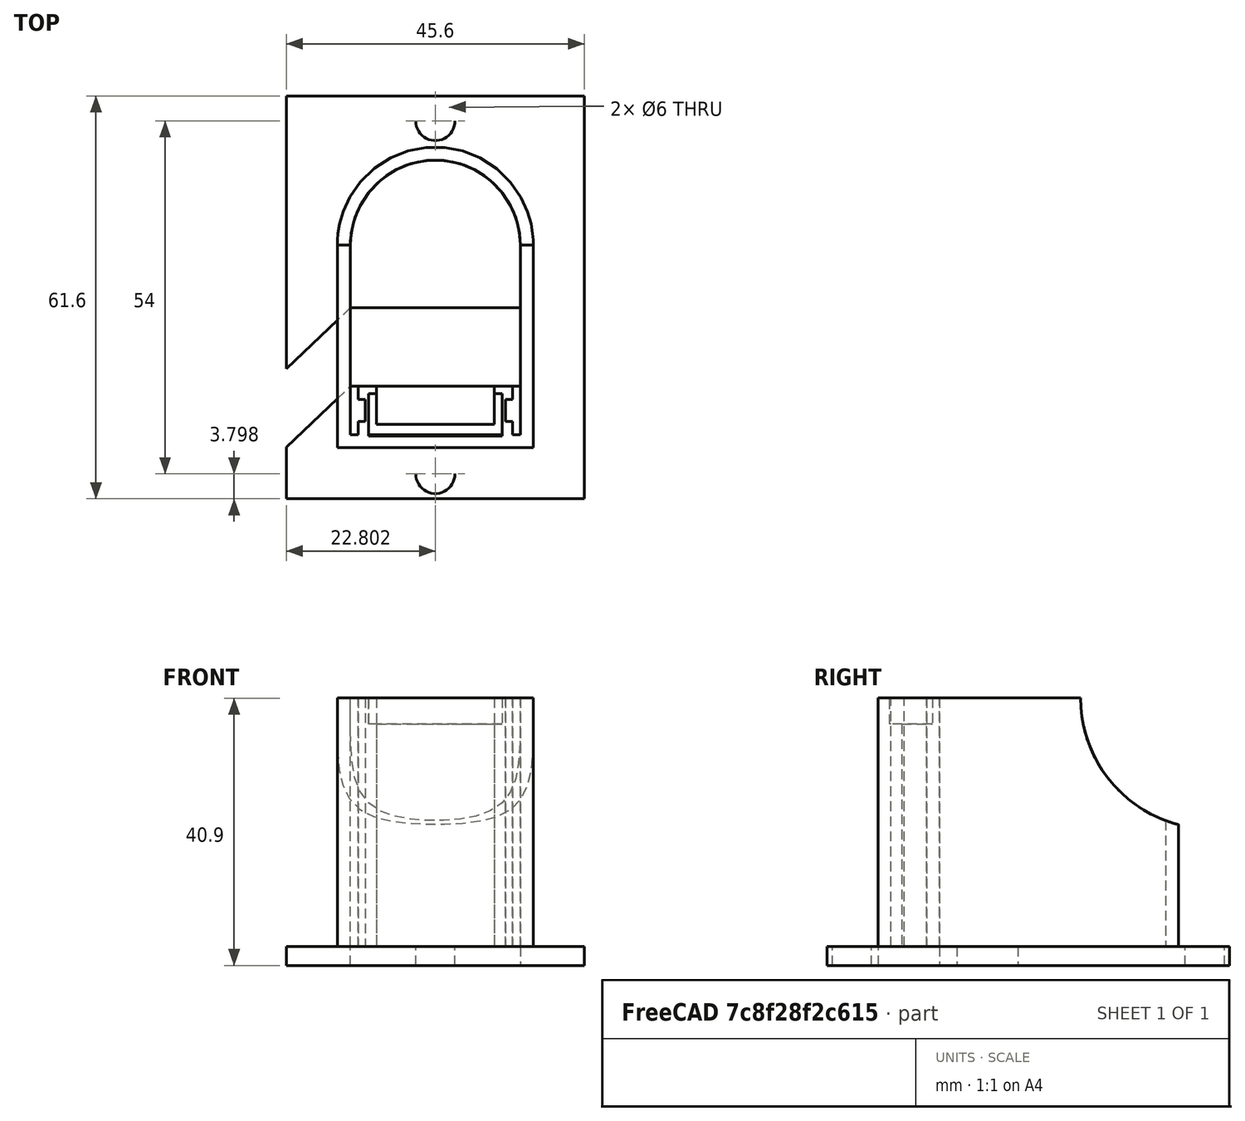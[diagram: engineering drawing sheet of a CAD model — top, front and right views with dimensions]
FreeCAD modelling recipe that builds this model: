
FCSTD DOCUMENT  (FreeCAD 0.18.4R)
Label: lamp.base.nest
License: All rights reserved
LicenseURL: http://en.wikipedia.org/wiki/All_rights_reserved
objects: Part::Extrusion×5, Part::Cut×5, Part::Feature×3, Part::Part2DObjectPython×3
note: 16 computed .brp shape members not serialized (recipe doc carries the construction recipe); baked Part::Feature solids carry a one-line shape summary decoded from their .brp

FEATURE [Part::Feature] Cut098001  label="Cut099"
  shape: bbox 45.84 x 61.84 x 41.04 mm, 66 faces (baked)
FEATURE [Part::Feature] Face042
  shape: bbox 0.04215 x 61.84 x 3.044 mm, 1 faces, 0 solids (baked)
FEATURE [Part::Extrusion] Extrusion069
  Base = -> Face042
  Dir = (-0.1,0,0)
  DirMode = 0
  FaceMakerClass = Part::FaceMakerBullseye
  LengthFwd = 0
  LengthRev = 0
  Solid = true
  Symmetric = false
FEATURE [Part::Cut] Cut098002
  Base = -> Cut098001
  Tool = -> Extrusion069
FEATURE [Part::Part2DObjectPython] Rectangle228  # Draft 2D object (typed FeaturePython)
  ChamferSize = 0
  Columns = 1
  FilletRadius = 0
  Height = 61.8
  Length = 3
  MakeFace = true
  Placement = pos=(-323.568,-186.112,4.34295) rot=(-1.1e-05,-1,1.1e-05;1.5708rad)
  Rows = 1
  Support = -> [Cut098002]
FEATURE [Part::Extrusion] Extrusion070
  Base = -> Rectangle228
  Dir = (0.1,0,0)
  DirMode = 0
  FaceMakerClass = Part::FaceMakerBullseye
  LengthFwd = 0
  LengthRev = 0
  Solid = true
  Symmetric = false
FEATURE [Part::Cut] Cut098003
  Base = -> Cut098002
  Tool = -> Extrusion070
FEATURE [Part::Part2DObjectPython] Rectangle229  # Draft 2D object (typed FeaturePython)
  ChamferSize = 0
  Columns = 1
  FilletRadius = 0
  Height = 8
  Length = 45.6
  MakeFace = true
  Placement = pos=(-323.468,-124.312,8.34159) rot=(-1,0,0;1.57082rad)
  Rows = 1
  Support = -> [Cut098003]
FEATURE [Part::Extrusion] Extrusion071
  Base = -> Rectangle229
  Dir = (0,-0.1,0)
  DirMode = 0
  FaceMakerClass = Part::FaceMakerBullseye
  LengthFwd = 0
  LengthRev = 0
  Solid = true
  Symmetric = false
FEATURE [Part::Cut] Cut098004
  Base = -> Cut098003
  Tool = -> Extrusion071
FEATURE [Part::Part2DObjectPython] Rectangle230  # Draft 2D object (typed FeaturePython)
  ChamferSize = 0
  Columns = 1
  FilletRadius = 0
  Height = 45.6
  Length = 10
  MakeFace = true
  Placement = pos=(-277.868,-186.112,2.34295) rot=(0.577346,-0.577346,0.577359;2.09438rad)
  Rows = 1
  Support = -> [Cut098004]
FEATURE [Part::Extrusion] Extrusion072
  Base = -> Rectangle230
  Dir = (0,0.1,0)
  DirMode = 0
  FaceMakerClass = Part::FaceMakerBullseye
  LengthFwd = 0
  LengthRev = 0
  Solid = true
  Symmetric = false
FEATURE [Part::Cut] Cut098005
  Base = -> Cut098004
  Tool = -> Extrusion072
FEATURE [Part::Feature] Face
  shape: bbox 45.64 x 61.64 x 0.0435 mm, 1 faces, 0 solids (baked)
FEATURE [Part::Extrusion] Extrusion
  Base = -> Face
  Dir = (0,2.19278e-06,0.1)
  DirMode = 0
  FaceMakerClass = Part::FaceMakerBullseye
  LengthFwd = 0
  LengthRev = 0
  Solid = true
  Symmetric = false
FEATURE [Part::Cut] Cut
  Base = -> Cut098005
  Tool = -> Extrusion
